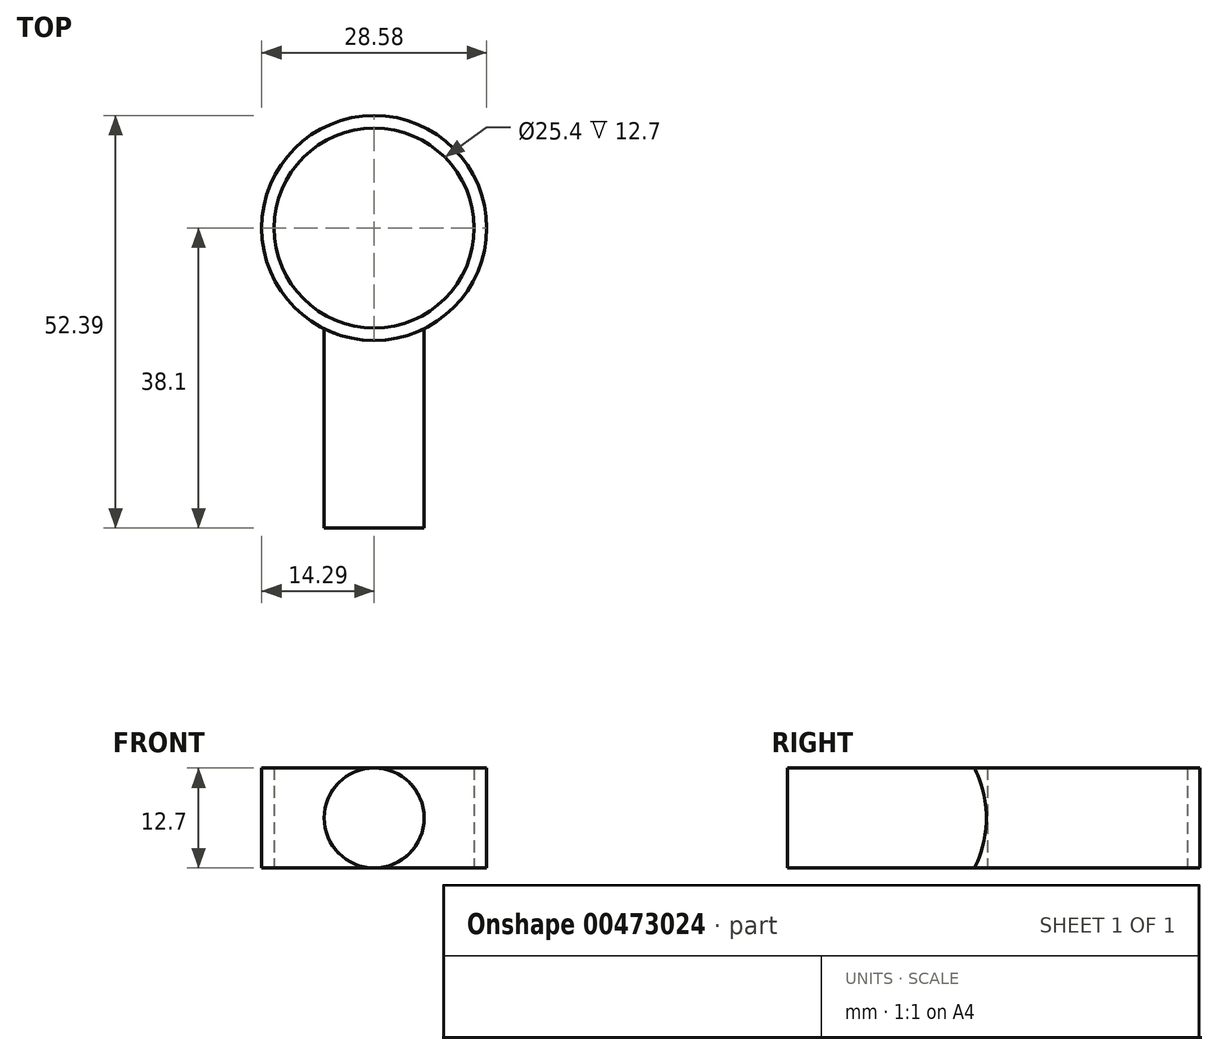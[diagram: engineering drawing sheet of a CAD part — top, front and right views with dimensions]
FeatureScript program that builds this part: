
annotation { "Feature Type Name" : "Feature", "Feature Type Description" : "" }
export const myFeature = defineFeature(function(context is Context, id is Id, definition is map)
    precondition{}
    {
        {
            var Q0;
            Q0=qCreatedBy(makeId("Front.planeOp"),FACE);
            var sketch = newSketch(context, id + "F0", { "sketchPlane" : qUnion([Q0])});
            skCircle(sketch, "E0", {"center": v(0, 0) * mm, "radius": 6.35 * mm});
            skSolve(sketch);
        }
        {
            var Q0;
            Q0=makeQuery(id+"F0.imprint","IMPRINT",FACE,{"disambiguationData":[TD([[makeQuery(id+"F0.imprint","IMPRINT",EDGE,{"derivedFrom":sQuery(id+"F0.wireOp",EDGE,"E0")}),1.0]])]});
            extrude(context, id + "F1", {"entities" : qUnion([Q0]), "depth" : 25.4 * mm});
        }
        {
            var Q0;
            Q0=qCreatedBy(makeId("Top.planeOp"),FACE);
            var sketch = newSketch(context, id + "F2", { "sketchPlane" : qUnion([Q0])});
            skLineSegment(sketch, "E1", {"start": v(0, 0) * mm, "end": v(0, 12.7) * mm});
            skCircle(sketch, "E2", {"center": v(0, 12.7) * mm, "radius": 12.7 * mm});
            skCircle(sketch, "E3", {"center": v(0, 12.7) * mm, "radius": 14.29 * mm});
            skSolve(sketch);
        }
        {
            var Q0;
            Q0=makeQuery(id+"F2.imprint","IMPRINT",FACE,{"disambiguationData":[TD([[makeQuery(id+"F2.imprint","IMPRINT",EDGE,{"derivedFrom":sQuery(id+"F2.wireOp",EDGE,"E2")}),-1.0]])]});
            extrude(context, id + "F3", {"entities" : qUnion([Q0]), "operationType" : NewBodyOperationType.ADD, "depth" : 6.35 * mm, "hasSecondDirection" : true, "secondDirectionOppositeDirection" : true, "secondDirectionDepth" : 6.35 * mm});
        }
    });
